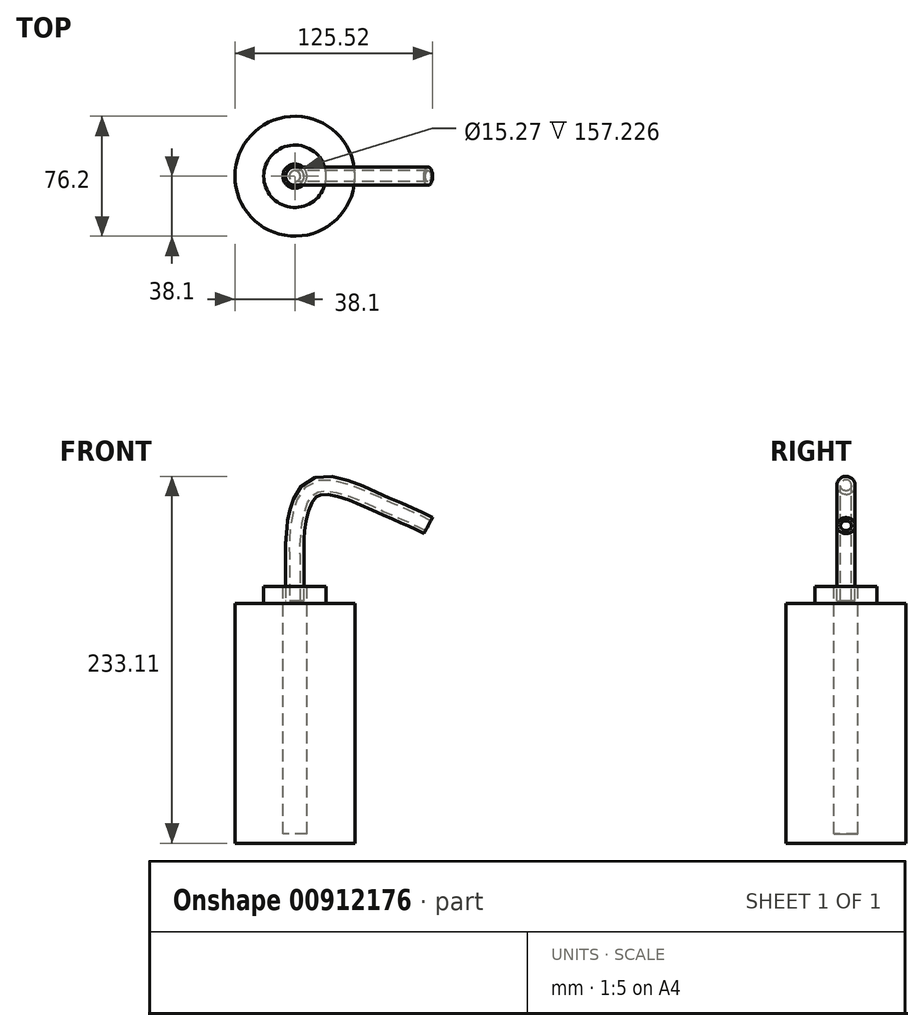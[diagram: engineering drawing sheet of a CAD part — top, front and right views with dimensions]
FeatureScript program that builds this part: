
annotation { "Feature Type Name" : "Feature", "Feature Type Description" : "" }
export const myFeature = defineFeature(function(context is Context, id is Id, definition is map)
    precondition{}
    {
        {
            var Q0;
            Q0=qCreatedBy(makeId("Right.planeOp"),FACE);
            var sketch = newSketch(context, id + "F0", { "sketchPlane" : qUnion([Q0])});
            skLineSegment(sketch, "E0", {"start": v(0, 0) * mm, "end": v(38.1, 0) * mm, "construction": true});
            skLineSegment(sketch, "E1", {"start": v(38.1, 0) * mm, "end": v(38.1, -76.2) * mm});
            skLineSegment(sketch, "E2", {"start": v(38.1, 0) * mm, "end": v(38.1, 76.2) * mm});
            skLineSegment(sketch, "E3", {"start": v(38.1, 76.2) * mm, "end": v(0, 76.2) * mm, "construction": true});
            skLineSegment(sketch, "E4", {"start": v(38.1, -76.2) * mm, "end": v(0, -76.2) * mm});
            skLineSegment(sketch, "E5", {"start": v(0, 76.2) * mm, "end": v(0, -76.2) * mm});
            skLineSegment(sketch, "E6", {"start": v(19.81, 76.2) * mm, "end": v(19.81, 87.03) * mm});
            skLineSegment(sketch, "E7", {"start": v(0, 87.03) * mm, "end": v(0, 76.2) * mm});
            skLineSegment(sketch, "E8", {"start": v(0, 87.03) * mm, "end": v(19.81, 87.03) * mm});
            skLineSegment(sketch, "E9", {"start": v(19.81, 76.2) * mm, "end": v(38.1, 76.2) * mm});
            skSolve(sketch);
        }
        {
            var Q0;
            Q0=makeQuery(id+"F0.imprint","IMPRINT",FACE,{"disambiguationData":[TD([[makeQuery(id+"F0.imprint","IMPRINT",EDGE,{"derivedFrom":sQuery(id+"F0.wireOp",EDGE,"E1")}),-1.0]])]});
            var Q1;
            Q1=sQuery(id+"F0.wireOp",EDGE,"E7");
            revolve(context, id + "F1", {"surfaceOperationType" : NewSurfaceOperationType.NEW, "entities" : qUnion([Q0]), "axis" : qUnion([Q1]), "revolveType" : RevolveType.FULL});
        }
        {
            var Q0;
            Q0=makeQuery(id+"F1.opRevolve","SWEPT_FACE",FACE,{"disambiguationData":[OSD([sQuery(id+"F0.wireOp",EDGE,"E8")])]});
            var sketch = newSketch(context, id + "F2", { "sketchPlane" : qUnion([Q0])});
            skCircle(sketch, "E10", {"center": v(0, 0) * mm, "radius": 7.63 * mm});
            skSolve(sketch);
        }
        {
            var Q0;
            Q0=makeQuery(id+"F2.imprint","IMPRINT",FACE,{"disambiguationData":[TD([[makeQuery(id+"F2.imprint","IMPRINT",EDGE,{"derivedFrom":sQuery(id+"F2.wireOp",EDGE,"E10")}),1.0]])]});
            extrude(context, id + "F3", {"entities" : qUnion([Q0]), "operationType" : NewBodyOperationType.REMOVE, "oppositeDirection" : true, "depth" : 157.23 * mm, "offsetDistance" : 25.4 * mm});
        }
        {
            var Q0;
            Q0=qCreatedBy(makeId("Front.planeOp"),FACE);
            var sketch = newSketch(context, id + "F4", { "sketchPlane" : qUnion([Q0])});
            skFitSpline(sketch, "E11", {"points": [v(0, 77.76) * mm, v(0, 115.27) * mm, v(9.78, 148.26) * mm, v(55.63, 138.8) * mm, v(84.63, 125.55) * mm], "startDerivative": vector(0, 530.3) * mm, "endDerivative": vector(122.7, -67.5) * mm});
            skSolve(sketch);
        }
        {
            var Q0;
            Q0=sQuery(id+"F4.wireOp",VERTEX,"E11.start");
            var Q1;
            Q1=sQuery(id+"F4.wireOp",EDGE,"E11");
            cPlane(context, id + "F5", {"entities" : qUnion([Q0, Q1]), "cplaneType" : CPlaneType.CURVE_POINT, "offset" : 25.4 * mm, "width" : 152.4 * mm, "height" : 152.4 * mm});
        }
        {
            var Q0;
            Q0=qCreatedBy(id+"F5.planeOp",FACE);
            var sketch = newSketch(context, id + "F6", { "sketchPlane" : qUnion([Q0])});
            skCircle(sketch, "E12", {"center": v(0, 0) * mm, "radius": 5.77 * mm});
            skCircle(sketch, "E13", {"center": v(0, 0) * mm, "radius": 3.5 * mm});
            skSolve(sketch);
        }
        {
            var Q0;
            Q0=makeQuery(id+"F6.imprint","IMPRINT",FACE,{"disambiguationData":[TD([[makeQuery(id+"F6.imprint","IMPRINT",EDGE,{"derivedFrom":sQuery(id+"F6.wireOp",EDGE,"E12")}),1.0]])]});
            var Q1;
            Q1=sQuery(id+"F4.wireOp",EDGE,"E11");
            sweep(context, id + "F7", {"profiles" : qUnion([Q0]), "path" : qUnion([Q1])});
        }
    });
